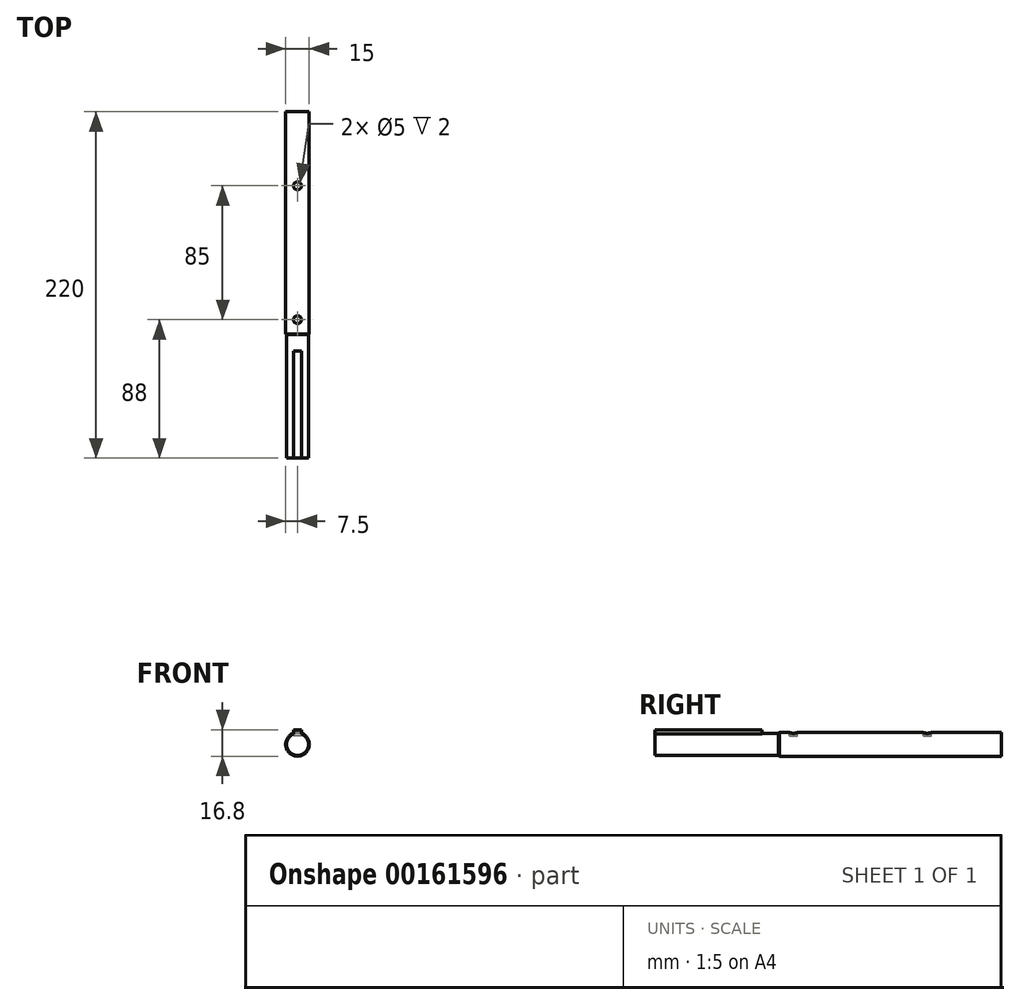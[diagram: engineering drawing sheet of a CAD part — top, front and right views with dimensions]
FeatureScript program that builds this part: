
annotation { "Feature Type Name" : "Feature", "Feature Type Description" : "" }
export const myFeature = defineFeature(function(context is Context, id is Id, definition is map)
    precondition{}
    {
        {
            var Q0;
            Q0=qCreatedBy(makeId("Front.planeOp"),FACE);
            var sketch = newSketch(context, id + "F0", { "sketchPlane" : qUnion([Q0])});
            skLineSegment(sketch, "E0", {"start": v(-2.5, 6.54) * mm, "end": v(-2.5, 9.3) * mm});
            skLineSegment(sketch, "E1", {"start": v(-2.5, 9.3) * mm, "end": v(2.5, 9.3) * mm});
            skLineSegment(sketch, "E2", {"start": v(2.5, 9.3) * mm, "end": v(2.5, 6.54) * mm});
            skArc(sketch, "E3", {"start": v(-2.5, 6.54) * mm, "mid": v(0, -7) * mm, "end": v(2.5, 6.54) * mm});
            skArc(sketch, "E4", {"start": v(2.5, 6.54) * mm, "mid": v(0, 7) * mm, "end": v(-2.5, 6.54) * mm, "construction": true});
            skSolve(sketch);
        }
        {
            var Q0;
            Q0 = qSketchRegion(id + "F0", true);
            extrude(context, id + "F1", {"entities" : qUnion([Q0]), "endBound" : BoundingType.SYMMETRIC, "depth" : 68 * mm});
        }
        {
            var Q0;
            Q0=makeQuery(id+"F1.opExtrude","CAP_FACE",FACE,{"disambiguationData":[OSD([sQuery(id+"F0.wireOp",EDGE,"E0"),sQuery(id+"F0.wireOp",EDGE,"E1"),sQuery(id+"F0.wireOp",EDGE,"E2"),sQuery(id+"F0.wireOp",EDGE,"E3")])],"isStart":true});
            var sketch = newSketch(context, id + "F2", { "sketchPlane" : qUnion([Q0])});
            skCircle(sketch, "E5", {"center": v(0, 0) * mm, "radius": 7 * mm});
            skSolve(sketch);
        }
        {
            var Q0;
            Q0 = qSketchRegion(id + "F2", true);
            extrude(context, id + "F3", {"entities" : qUnion([Q0]), "operationType" : NewBodyOperationType.ADD, "depth" : 10 * mm});
        }
        {
            var Q0;
            Q0=makeQuery(id+"F3.opExtrude","CAP_FACE",FACE,{"disambiguationData":[OSD([sQuery(id+"F2.wireOp",EDGE,"E5")])],"isStart":false});
            var sketch = newSketch(context, id + "F4", { "sketchPlane" : qUnion([Q0])});
            skCircle(sketch, "E6", {"center": v(0, 0) * mm, "radius": 7.5 * mm});
            skSolve(sketch);
        }
        {
            var Q0;
            Q0 = qSketchRegion(id + "F4", true);
            extrude(context, id + "F5", {"entities" : qUnion([Q0]), "operationType" : NewBodyOperationType.ADD, "depth" : 142 * mm});
        }
        {
            var Q0;
            Q0=qCreatedBy(makeId("Top.planeOp"),FACE);
            cPlane(context, id + "F6", {"entities" : qUnion([Q0]), "cplaneType" : CPlaneType.OFFSET, "offset" : 7.5 * mm, "width" : 150 * mm, "height" : 150 * mm});
        }
        {
            var Q0;
            Q0=qCreatedBy(id+"F6.planeOp",FACE);
            var sketch = newSketch(context, id + "F7", { "sketchPlane" : qUnion([Q0])});
            skCircle(sketch, "E7", {"center": v(0, 54) * mm, "radius": 2.5 * mm});
            skCircle(sketch, "E8", {"center": v(0, 139) * mm, "radius": 2.5 * mm});
            skSolve(sketch);
        }
        {
            var Q0;
            Q0 = qSketchRegion(id + "F7", true);
            extrude(context, id + "F8", {"entities" : qUnion([Q0]), "operationType" : NewBodyOperationType.REMOVE, "oppositeDirection" : true, "depth" : 2 * mm});
        }
        {
            var Q0;
            Q0=makeQuery(id+"F5.opExtrude","CAP_EDGE",EDGE,{"disambiguationData":[OSD([sQuery(id+"F4.wireOp",EDGE,"E6")])],"isStart":true});
            chamfer(context, id + "F9", {"entities" : qUnion([Q0]), "width" : 1 * mm, "tangentPropagation" : true});
        }
    });
